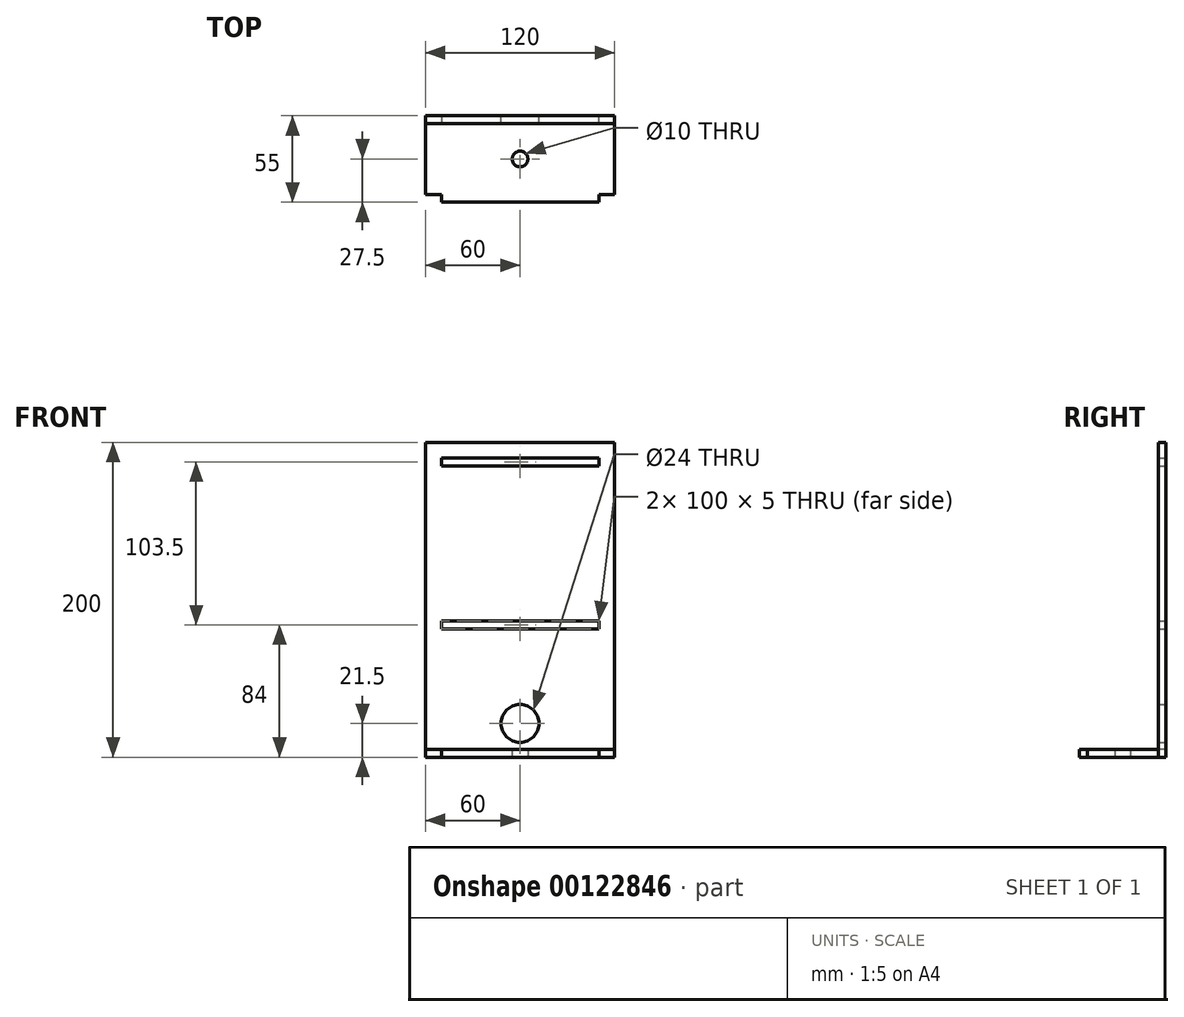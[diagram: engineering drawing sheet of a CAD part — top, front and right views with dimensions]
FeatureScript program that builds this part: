
annotation { "Feature Type Name" : "Feature", "Feature Type Description" : "" }
export const myFeature = defineFeature(function(context is Context, id is Id, definition is map)
    precondition{}
    {
        {
            var Q0;
            Q0=qCreatedBy(makeId("Front.planeOp"),FACE);
            var sketch = newSketch(context, id + "F0", { "sketchPlane" : qUnion([Q0])});
            skLineSegment(sketch, "E0.bottom", {"start": v(0, 0) * mm, "end": v(120, 0) * mm});
            skLineSegment(sketch, "E0.top", {"start": v(0, 200) * mm, "end": v(120, 200) * mm});
            skLineSegment(sketch, "E0.left", {"start": v(0, 0) * mm, "end": v(0, 200) * mm});
            skLineSegment(sketch, "E0.right", {"start": v(120, 0) * mm, "end": v(120, 200) * mm});
            skLineSegment(sketch, "E1.bottom", {"start": v(10, 190) * mm, "end": v(110, 190) * mm});
            skLineSegment(sketch, "E1.top", {"start": v(10, 185) * mm, "end": v(110, 185) * mm});
            skLineSegment(sketch, "E1.left", {"start": v(10, 190) * mm, "end": v(10, 185) * mm});
            skLineSegment(sketch, "E1.right", {"start": v(110, 190) * mm, "end": v(110, 185) * mm});
            skLineSegment(sketch, "E2.bottom", {"start": v(10, 86.5) * mm, "end": v(110, 86.5) * mm});
            skLineSegment(sketch, "E2.top", {"start": v(10, 81.5) * mm, "end": v(110, 81.5) * mm});
            skLineSegment(sketch, "E2.left", {"start": v(10, 86.5) * mm, "end": v(10, 81.5) * mm});
            skLineSegment(sketch, "E2.right", {"start": v(110, 86.5) * mm, "end": v(110, 81.5) * mm});
            skCircle(sketch, "E3", {"center": v(60, 21.5) * mm, "radius": 12 * mm});
            skSolve(sketch);
        }
        {
            var Q0;
            Q0 = qSketchRegion(id + "F0", true);
            extrude(context, id + "F1", {"entities" : qUnion([Q0]), "depth" : 5 * mm});
        }
        {
            var Q0;
            Q0=qCreatedBy(makeId("Top.planeOp"),FACE);
            var sketch = newSketch(context, id + "F2", { "sketchPlane" : qUnion([Q0])});
            skLineSegment(sketch, "E4", {"start": v(10, 0) * mm, "end": v(10, -5) * mm});
            skLineSegment(sketch, "E5", {"start": v(10, -5) * mm, "end": v(0, -5) * mm});
            skLineSegment(sketch, "E6", {"start": v(0, -5) * mm, "end": v(0, -50) * mm});
            skLineSegment(sketch, "E7", {"start": v(0, -50) * mm, "end": v(10, -50) * mm});
            skLineSegment(sketch, "E8", {"start": v(10, -50) * mm, "end": v(10, -55) * mm});
            skLineSegment(sketch, "E9", {"start": v(10, -55) * mm, "end": v(110, -55) * mm});
            skLineSegment(sketch, "E10", {"start": v(110, -55) * mm, "end": v(110, -50) * mm});
            skLineSegment(sketch, "E11", {"start": v(110, -50) * mm, "end": v(120, -50) * mm});
            skLineSegment(sketch, "E12", {"start": v(120, -50) * mm, "end": v(120, -5) * mm});
            skLineSegment(sketch, "E13", {"start": v(120, -5) * mm, "end": v(110, -5) * mm});
            skLineSegment(sketch, "E14", {"start": v(110, -5) * mm, "end": v(110, 0) * mm});
            skLineSegment(sketch, "E15", {"start": v(110, 0) * mm, "end": v(10, 0) * mm});
            skCircle(sketch, "E16", {"center": v(60, -27.5) * mm, "radius": 5 * mm});
            skSolve(sketch);
        }
        {
            var Q0;
            Q0 = qSketchRegion(id + "F2", true);
            extrude(context, id + "F3", {"entities" : qUnion([Q0]), "depth" : 5 * mm});
        }
    });
